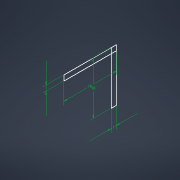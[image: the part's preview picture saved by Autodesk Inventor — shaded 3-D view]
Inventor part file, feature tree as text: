
AUTODESK INVENTOR PART (.ipt)
format: ipt  version: 2021 (Build 250183000, 183)  size: 112,640 bytes
history: native  units: mm
features: sketch x3, hole x2, other x1, extrude x1
ambient origin geometry x8: Origin, YZ Plane, XZ Plane, XY Plane, X Axis, Y Axis, Z Axis, Center Point
bodies: Body1 (feature_tree)
feature tree (7):
  other  "ソリッド1"
  extrude  "押し出し1"  Depth=1.0mm
  hole  "穴1"  [1 undecoded]
  hole  "穴2"  [1 undecoded]
  sketch  "スケッチ1"
  sketch  "スケッチ2"
  sketch  "スケッチ3"
note: 2 required parameter values undecoded (feature->parameter linkage not recoverable at this tier; creation-order binding heuristic only, values carry confidence <= 0.55)
